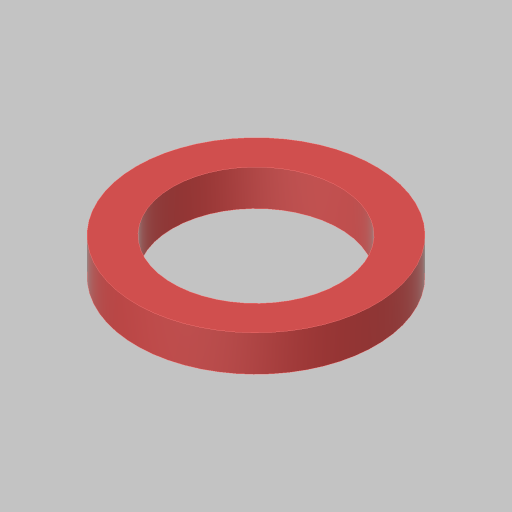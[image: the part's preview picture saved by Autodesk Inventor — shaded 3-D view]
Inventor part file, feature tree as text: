
AUTODESK INVENTOR PART (.ipt)
format: ipt  version: 2023.5 (Build 275446000, 446)  size: 95,744 bytes
history: native  units: in
note: dims shown in document units (in); Inventor stores cm internally (conversion verified against a paired STEP export)
features: extrude x1, sketch x1
ambient origin geometry x8: Origin, YZ Plane, XZ Plane, XY Plane, X Axis, Y Axis, Z Axis, Center Point
bodies: Solid1 (feature_tree)
feature tree (2):
  extrude  "Extrusion1"  Depth=0.125in
  sketch  "Sketch1"  dims[d0=0.58in d1=0.125in d2=0.125in d3=0.0in]
